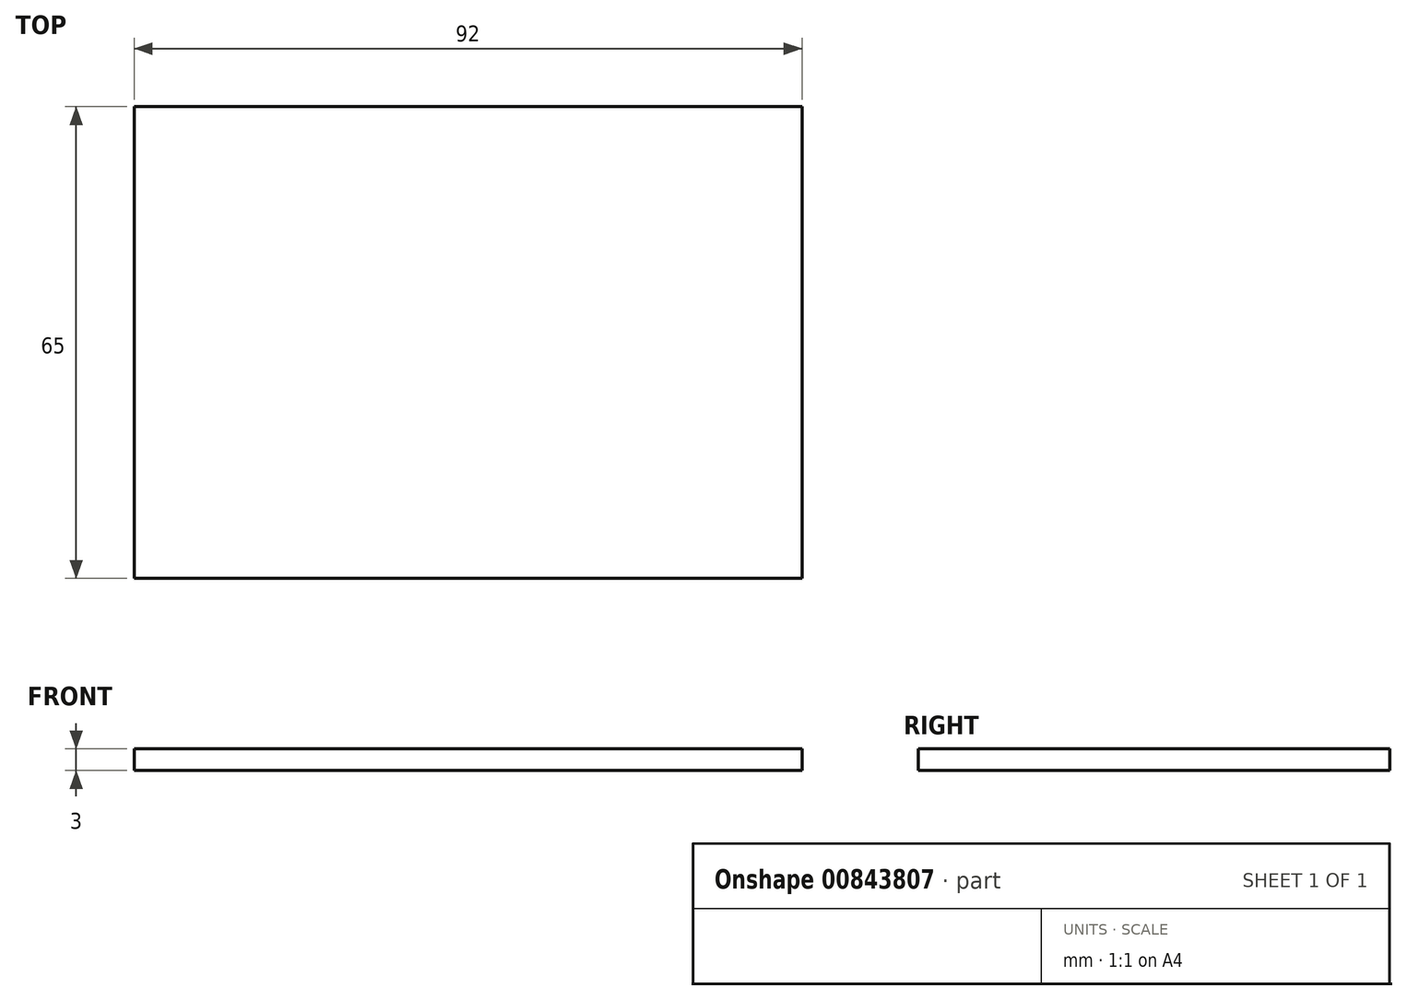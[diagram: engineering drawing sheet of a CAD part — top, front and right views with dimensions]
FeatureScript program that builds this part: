
annotation { "Feature Type Name" : "Feature", "Feature Type Description" : "" }
export const myFeature = defineFeature(function(context is Context, id is Id, definition is map)
    precondition{}
    {
        {
            var Q0;
            Q0=qCreatedBy(makeId("Top.planeOp"),FACE);
            var sketch = newSketch(context, id + "F0", { "sketchPlane" : qUnion([Q0])});
            skLineSegment(sketch, "E0.bottom", {"start": v(-50.25, -44.45) * mm, "end": v(41.75, -44.45) * mm});
            skLineSegment(sketch, "E0.top", {"start": v(-50.25, 20.55) * mm, "end": v(41.75, 20.55) * mm});
            skLineSegment(sketch, "E0.left", {"start": v(-50.25, -44.45) * mm, "end": v(-50.25, 20.55) * mm});
            skLineSegment(sketch, "E0.right", {"start": v(41.75, -44.45) * mm, "end": v(41.75, 20.55) * mm});
            skSolve(sketch);
        }
        {
            var Q0;
            Q0=makeQuery(id+"F0.imprint","IMPRINT",FACE,{"disambiguationData":[TD([[makeQuery(id+"F0.imprint","IMPRINT",EDGE,{"derivedFrom":sQuery(id+"F0.wireOp",EDGE,"E0.bottom")}),1.0]])]});
            extrude(context, id + "F1", {"entities" : qUnion([Q0]), "depth" : 3 * mm, "offsetDistance" : 25 * mm});
        }
    });
